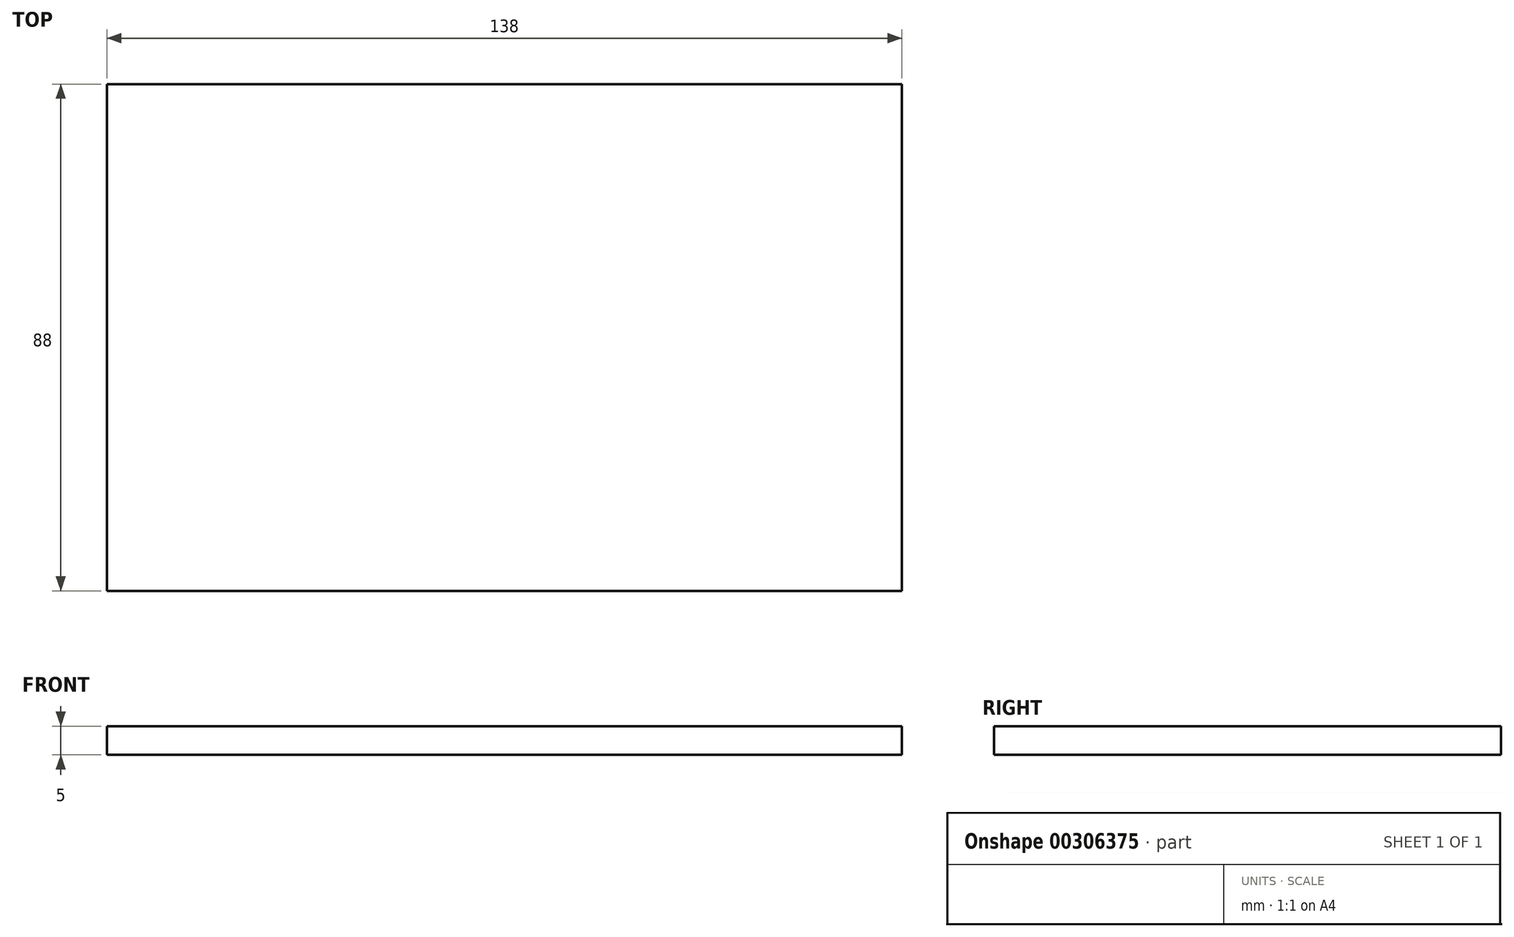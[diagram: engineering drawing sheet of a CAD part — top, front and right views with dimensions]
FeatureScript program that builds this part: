
annotation { "Feature Type Name" : "Feature", "Feature Type Description" : "" }
export const myFeature = defineFeature(function(context is Context, id is Id, definition is map)
    precondition{}
    {
        {
            var Q0;
            Q0=qCreatedBy(makeId("Front.planeOp"),FACE);
            var sketch = newSketch(context, id + "F0", { "sketchPlane" : qUnion([Q0])});
            skLineSegment(sketch, "E0.bottom", {"start": v(-75.7, 5) * mm, "end": v(62.3, 5) * mm});
            skLineSegment(sketch, "E0.top", {"start": v(-75.7, 0) * mm, "end": v(62.3, 0) * mm});
            skLineSegment(sketch, "E0.left", {"start": v(-75.7, 5) * mm, "end": v(-75.7, 0) * mm});
            skLineSegment(sketch, "E0.right", {"start": v(62.3, 5) * mm, "end": v(62.3, 0) * mm});
            skSolve(sketch);
        }
        {
            var Q0;
            Q0=makeQuery(id+"F0.imprint","IMPRINT",FACE,{"disambiguationData":[TD([[makeQuery(id+"F0.imprint","IMPRINT",EDGE,{"derivedFrom":sQuery(id+"F0.wireOp",EDGE,"E0.bottom")}),-1.0]])]});
            extrude(context, id + "F1", {"entities" : qUnion([Q0]), "depth" : 88 * mm});
        }
    });
